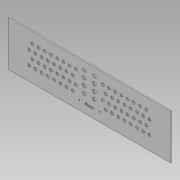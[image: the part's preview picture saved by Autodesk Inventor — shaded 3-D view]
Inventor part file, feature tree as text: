
AUTODESK INVENTOR PART (.ipt)
format: ipt  version: 2021.4 (Build 254397000, 397)  size: 423,936 bytes
history: native  units: in
note: dims shown in document units (in); Inventor stores cm internally (conversion verified against a paired STEP export)
features: extrude x4, sketch x4
ambient origin geometry x8: Origin, YZ Plane, XZ Plane, XY Plane, X Axis, Y Axis, Z Axis, Center Point
bodies: Solid1 (feature_tree)
feature tree (8):
  extrude  "Extrusion1"  Depth=5.2362in
  extrude  "Extrusion2"  Depth=0.1181in
  extrude  "Extrusion3"  Depth=0.5906in
  extrude  "Extrusion4"  Depth=0.0591in
  sketch  "Sketch1"  dims[d0=18.9764in d1=5.2362in]
  sketch  "Sketch2"  dims[d2=0.1181in d3=0.0in d4=15.5118in]
  sketch  "Sketch3"  dims[d5=3.937in d6=0.5906in]
  sketch  "Sketch4"  dims[d7=0.1969in d12=0.3902in d13=0.1531in d14=0.3902in d15=0.1531in d16=0.3902in d17=0.1531in d19=0.7874in d20=0.7874in d21=0.1181in d22=0.0in d23=15.5118in d24=3.937in d25=0.7874in d29=0.3169in d30=0.2854in d31=0.3169in d32=0.2854in d33=0.3169in d34=0.2854in d35=0.3169in d36=0.2854in d37=0.3169in d38=0.2854in d39=0.3169in d40=0.2854in d41=0.3169in d42=0.2854in d44=0.7283in d45=0.7283in d46=0.7283in d47=0.7283in d48=0.7283in d49=0.7283in d50=0.3169in d73=1.3484in d74=0.2854in d75=0.3169in d76=0.2854in d77=0.3169in d78=0.2854in d79=0.3169in d80=0.2854in d81=0.3169in d82=0.2854in d83=0.3169in d84=0.2854in d85=0.3169in d86=0.2854in d87=0.3169in d88=0.2854in d89=0.7283in d90=0.7283in d91=0.7283in d92=0.7283in d93=0.7283in d94=0.7283in d95=0.7283in d96=0.3169in d98=0.3169in d100=0.3169in d102=0.3169in d104=0.3169in d106=0.3169in d108=0.3169in d110=0.3169in d112=0.7283in d113=0.7283in d114=0.7283in d115=0.7283in d116=0.7283in d117=0.7283in d118=0.7283in d119=0.3169in d121=0.3169in d123=0.3169in d125=0.3169in d127=0.3169in d129=0.3169in d131=0.3169in d133=0.3169in d135=0.7283in d136=0.7283in d137=0.7283in d138=0.7283in d139=0.7283in d140=0.7283in d141=0.7283in d142=0.2854in d143=0.9843in d144=0.2854in d145=0.2854in d146=0.2854in d147=0.2854in d148=0.2854in d149=0.2854in d150=0.2854in d151=0.2854in d152=0.2854in d153=0.2854in d154=0.2854in d155=0.2854in d156=0.2854in d157=0.2854in d158=0.2854in d159=1.3484in d160=0.1181in d161=0.0in d162=0.9843in d163=0.1969in d164=1.5748in d165=1.1811in d166=0.1181in d167=0.689in d168=0.1181in d169=0.0in d170=0.0591in d172=0.127in]
